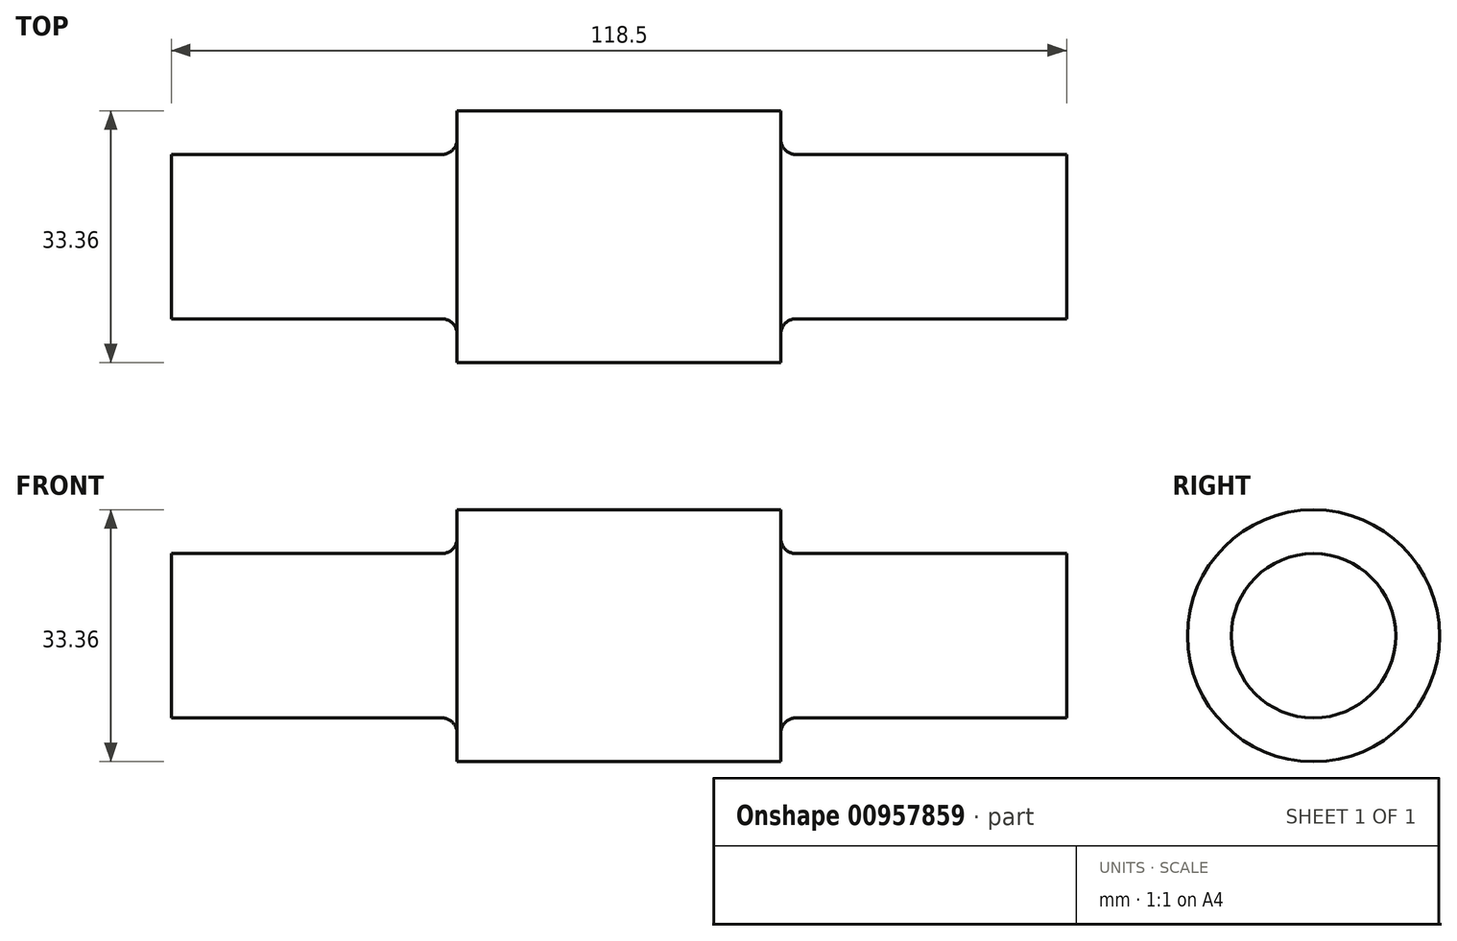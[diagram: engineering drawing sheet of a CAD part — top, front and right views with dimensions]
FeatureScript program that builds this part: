
annotation { "Feature Type Name" : "Feature", "Feature Type Description" : "" }
export const myFeature = defineFeature(function(context is Context, id is Id, definition is map)
    precondition{}
    {
        {
            var Q0;
            Q0=qCreatedBy(makeId("Front.planeOp"),FACE);
            var sketch = newSketch(context, id + "F0", { "sketchPlane" : qUnion([Q0])});
            skLineSegment(sketch, "E0", {"start": v(-59.25, 0) * mm, "end": v(-59.25, 10.89) * mm});
            skLineSegment(sketch, "E1", {"start": v(-59.25, 10.89) * mm, "end": v(-23.42, 10.89) * mm});
            skLineSegment(sketch, "E2", {"start": v(-21.42, 12.89) * mm, "end": v(-21.42, 16.68) * mm});
            skLineSegment(sketch, "E3", {"start": v(-21.42, 16.68) * mm, "end": v(0, 16.68) * mm});
            skPoint(sketch, "E4.visualSharp", {"position": v(-21.42, 10.89) * mm});
            skArc(sketch, "E4.filletArc", {"start": v(-23.42, 10.89) * mm, "mid": v(-22, 11.47) * mm, "end": v(-21.42, 12.89) * mm});
            skLineSegment(sketch, "E5.MirrorCS", {"start": v(21.42, 16.68) * mm, "end": v(0, 16.68) * mm});
            skLineSegment(sketch, "E6.MirrorCS", {"start": v(21.42, 12.89) * mm, "end": v(21.42, 16.68) * mm});
            skPoint(sketch, "E7.MirrorP", {"position": v(21.42, 10.89) * mm});
            skLineSegment(sketch, "E8.MirrorCS", {"start": v(59.25, 10.89) * mm, "end": v(23.42, 10.89) * mm});
            skArc(sketch, "E9.MirrorCS", {"start": v(23.42, 10.89) * mm, "mid": v(22, 11.47) * mm, "end": v(21.42, 12.89) * mm});
            skLineSegment(sketch, "E10", {"start": v(59.25, 10.89) * mm, "end": v(59.25, 0) * mm});
            skLineSegment(sketch, "E11", {"start": v(59.25, 0) * mm, "end": v(-59.25, 0) * mm});
            skSolve(sketch);
        }
        {
            var Q0;
            Q0=makeQuery(id+"F0.imprint","IMPRINT",FACE,{"disambiguationData":[TD([[makeQuery(id+"F0.imprint","IMPRINT",EDGE,{"derivedFrom":sQuery(id+"F0.wireOp",EDGE,"E0")}),-1.0]])]});
            var Q1;
            Q1=sQuery(id+"F0.wireOp",EDGE,"E11");
            revolve(context, id + "F1", {"surfaceOperationType" : NewSurfaceOperationType.NEW, "entities" : qUnion([Q0]), "axis" : qUnion([Q1]), "revolveType" : RevolveType.FULL});
        }
    });
